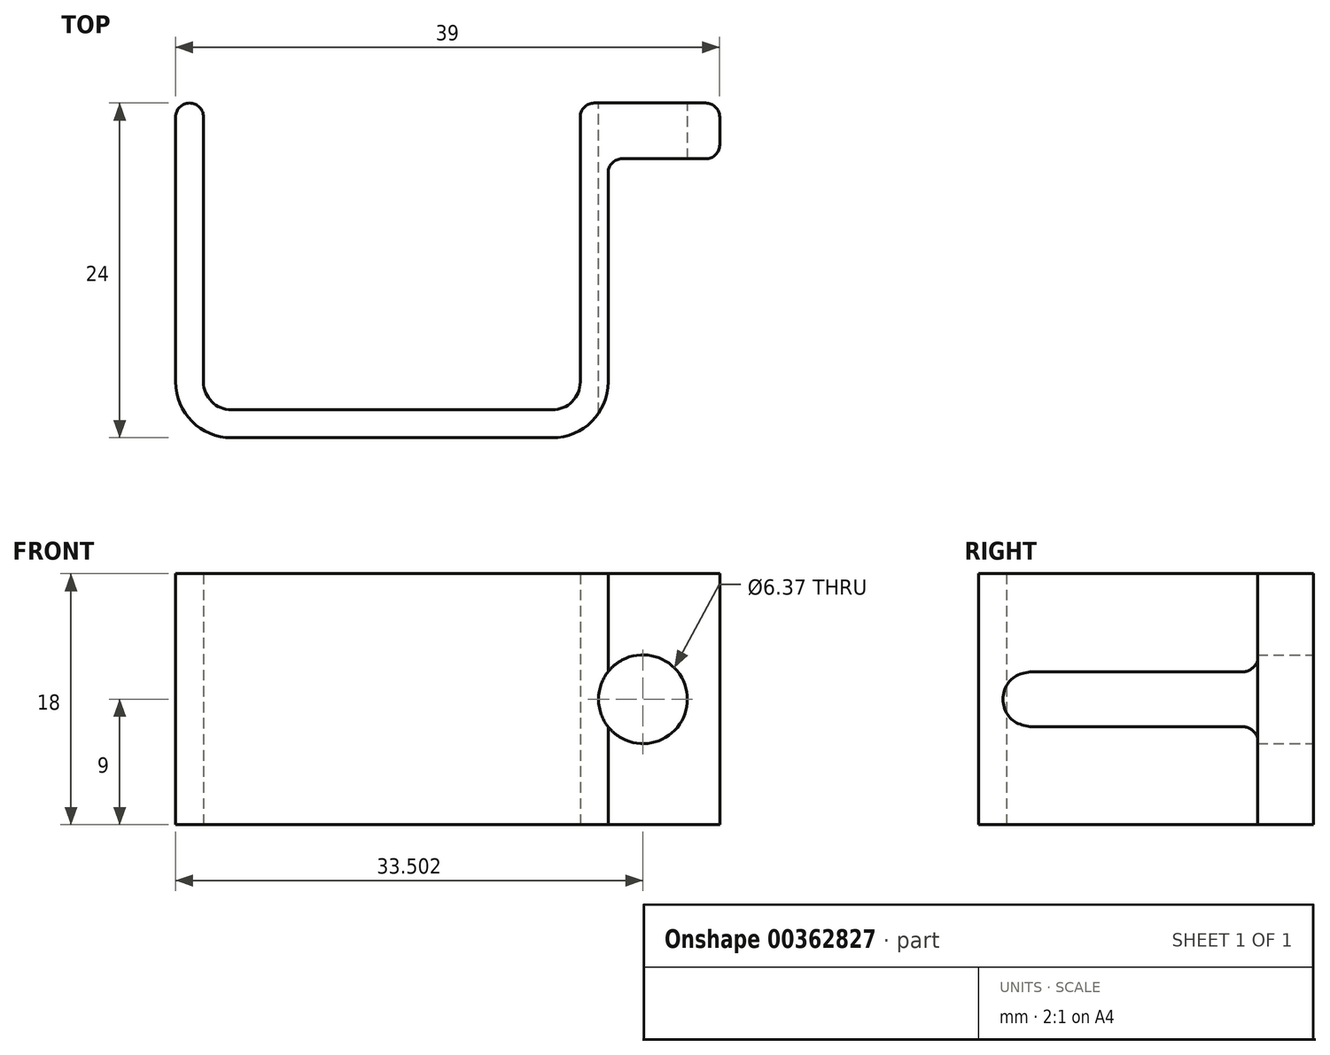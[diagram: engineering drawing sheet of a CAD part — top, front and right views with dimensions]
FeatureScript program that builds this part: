
annotation { "Feature Type Name" : "Feature", "Feature Type Description" : "" }
export const myFeature = defineFeature(function(context is Context, id is Id, definition is map)
    precondition{}
    {
        {
            var Q0;
            Q0=qCreatedBy(makeId("Top.planeOp"),FACE);
            var sketch = newSketch(context, id + "F0", { "sketchPlane" : qUnion([Q0])});
            skLineSegment(sketch, "E0", {"start": v(-16.25, 13.17) * mm, "end": v(-16.25, 13.17) * mm});
            skLineSegment(sketch, "E1", {"start": v(-15.25, 12.17) * mm, "end": v(-15.25, -6.83) * mm});
            skLineSegment(sketch, "E2", {"start": v(-13.25, -8.83) * mm, "end": v(9.75, -8.83) * mm});
            skLineSegment(sketch, "E3", {"start": v(11.75, -6.83) * mm, "end": v(11.75, 12.17) * mm});
            skLineSegment(sketch, "E4", {"start": v(12.75, 13.17) * mm, "end": v(20.75, 13.17) * mm});
            skLineSegment(sketch, "E5", {"start": v(21.75, 12.17) * mm, "end": v(21.75, 10.17) * mm});
            skLineSegment(sketch, "E6", {"start": v(20.75, 9.17) * mm, "end": v(14.75, 9.17) * mm});
            skLineSegment(sketch, "E7", {"start": v(13.75, 8.17) * mm, "end": v(13.75, -6.83) * mm});
            skLineSegment(sketch, "E8", {"start": v(9.75, -10.83) * mm, "end": v(-13.25, -10.83) * mm});
            skLineSegment(sketch, "E9", {"start": v(-17.25, -6.83) * mm, "end": v(-17.25, 12.17) * mm});
            skPoint(sketch, "E10.visualSharp", {"position": v(-15.25, -8.83) * mm});
            skArc(sketch, "E10.filletArc", {"start": v(-15.25, -6.83) * mm, "mid": v(-14.66, -8.24) * mm, "end": v(-13.25, -8.83) * mm});
            skPoint(sketch, "E11.visualSharp", {"position": v(11.75, -8.83) * mm});
            skArc(sketch, "E11.filletArc", {"start": v(9.75, -8.83) * mm, "mid": v(11.17, -8.24) * mm, "end": v(11.75, -6.83) * mm});
            skPoint(sketch, "E12.visualSharp", {"position": v(-17.25, -10.83) * mm});
            skArc(sketch, "E12.filletArc", {"start": v(-17.25, -6.83) * mm, "mid": v(-16.07, -9.66) * mm, "end": v(-13.25, -10.83) * mm});
            skPoint(sketch, "E13.visualSharp", {"position": v(13.75, -10.83) * mm});
            skArc(sketch, "E13.filletArc", {"start": v(9.75, -10.83) * mm, "mid": v(12.58, -9.66) * mm, "end": v(13.75, -6.83) * mm});
            skLineSegment(sketch, "E14", {"start": v(16.25, 9.17) * mm, "end": v(16.25, 13.17) * mm, "construction": true});
            skLineSegment(sketch, "E15", {"start": v(13.05, 13.17) * mm, "end": v(13.05, -9.09) * mm, "construction": true});
            skLineSegment(sketch, "E16", {"start": v(19.45, 9.17) * mm, "end": v(19.45, 13.17) * mm, "construction": true});
            skPoint(sketch, "E17.visualSharp", {"position": v(13.75, 9.17) * mm});
            skArc(sketch, "E17.filletArc", {"start": v(14.75, 9.17) * mm, "mid": v(14.05, 8.88) * mm, "end": v(13.75, 8.17) * mm});
            skPoint(sketch, "E18.visualSharp", {"position": v(21.75, 9.17) * mm});
            skArc(sketch, "E18.filletArc", {"start": v(20.75, 9.17) * mm, "mid": v(21.46, 9.47) * mm, "end": v(21.75, 10.17) * mm});
            skPoint(sketch, "E19.visualSharp", {"position": v(21.75, 13.17) * mm});
            skArc(sketch, "E19.filletArc", {"start": v(21.75, 12.17) * mm, "mid": v(21.46, 12.88) * mm, "end": v(20.75, 13.17) * mm});
            skPoint(sketch, "E20.visualSharp", {"position": v(-15.25, 13.17) * mm});
            skArc(sketch, "E20.filletArc", {"start": v(-15.25, 12.17) * mm, "mid": v(-15.54, 12.88) * mm, "end": v(-16.25, 13.17) * mm});
            skPoint(sketch, "E21.visualSharp", {"position": v(-17.25, 13.17) * mm});
            skArc(sketch, "E21.filletArc", {"start": v(-16.25, 13.17) * mm, "mid": v(-16.95, 12.88) * mm, "end": v(-17.25, 12.17) * mm});
            skPoint(sketch, "E22.visualSharp", {"position": v(11.75, 13.17) * mm});
            skArc(sketch, "E22.filletArc", {"start": v(12.75, 13.17) * mm, "mid": v(12.05, 12.88) * mm, "end": v(11.75, 12.17) * mm});
            skSolve(sketch);
        }
        {
            var Q0;
            Q0 = qSketchRegion(id + "F0", true);
            extrude(context, id + "F1", {"entities" : qUnion([Q0]), "depth" : 18 * mm});
        }
        {
            var Q0;
            Q0=makeQuery(id+"F1.opExtrude","SWEPT_FACE",FACE,{"disambiguationData":[OSD([sQuery(id+"F0.wireOp",EDGE,"E4")])]});
            var sketch = newSketch(context, id + "F2", { "sketchPlane" : qUnion([Q0])});
            skLineSegment(sketch, "E23", {"start": v(-16.25, 0) * mm, "end": v(-16.25, 18) * mm, "construction": true});
            skCircle(sketch, "E24", {"center": v(-16.25, 9) * mm, "radius": 3.18 * mm});
            skLineSegment(sketch, "E25", {"start": v(-13.07, 0) * mm, "end": v(-13.07, 9) * mm, "construction": true});
            skPoint(sketch, "E25.endSnap0", {"position": v(-12.75, 9) * mm});
            skSolve(sketch);
        }
        {
            var Q0;
            Q0 = qSketchRegion(id + "F2", true);
            extrude(context, id + "F3", {"entities" : qUnion([Q0]), "operationType" : NewBodyOperationType.REMOVE, "oppositeDirection" : true, "depth" : 25 * mm});
        }
    });
